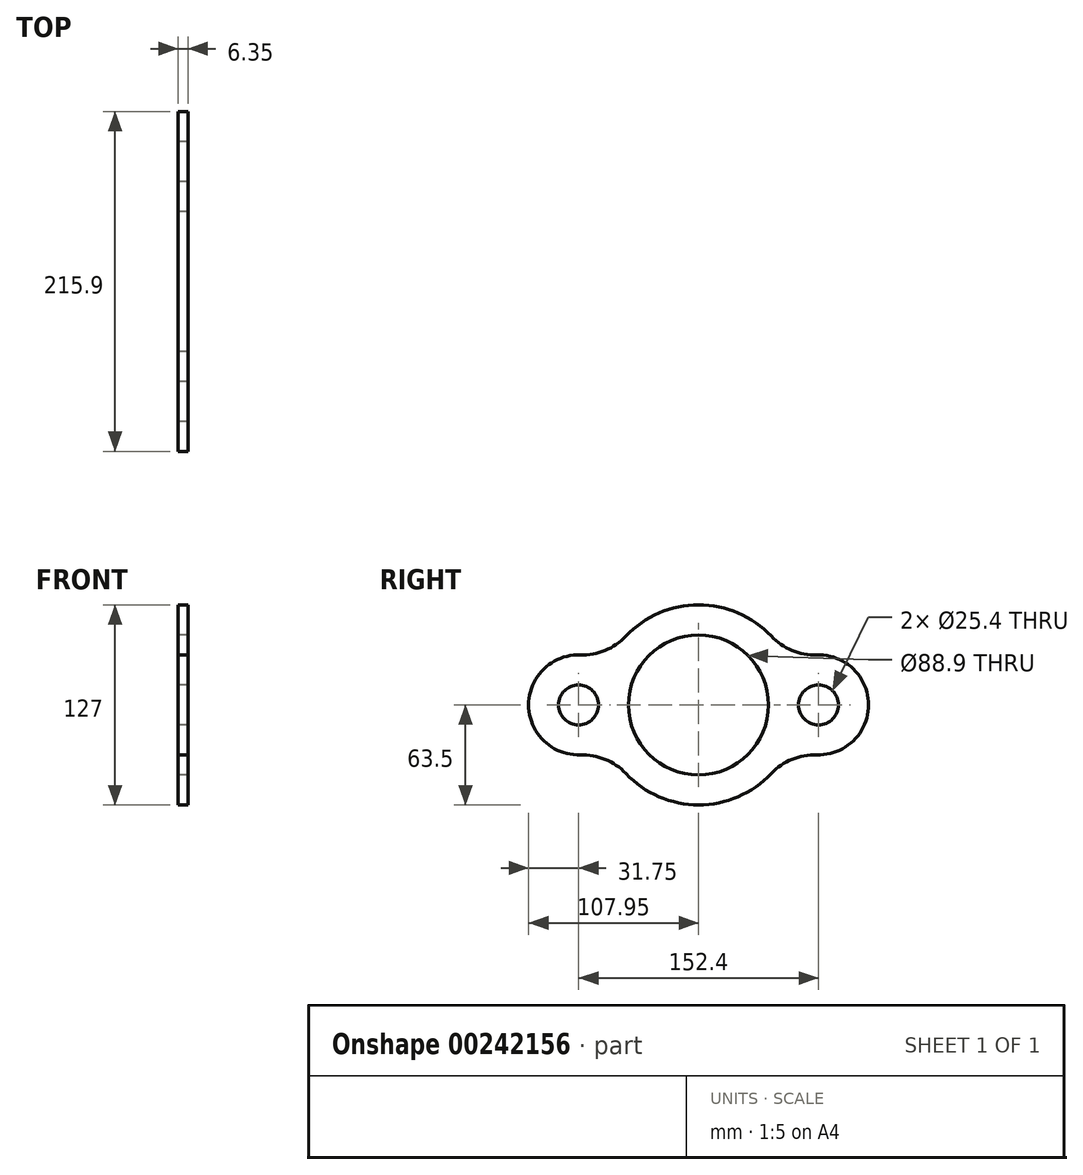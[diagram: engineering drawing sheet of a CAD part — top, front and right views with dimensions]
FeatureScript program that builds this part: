
annotation { "Feature Type Name" : "Feature", "Feature Type Description" : "" }
export const myFeature = defineFeature(function(context is Context, id is Id, definition is map)
    precondition{}
    {
        {
            var Q0;
            Q0=qCreatedBy(makeId("Right.planeOp"),FACE);
            var sketch = newSketch(context, id + "F0", { "sketchPlane" : qUnion([Q0])});
            skArc(sketch, "E0", {"start": v(46.14, 43.63) * mm, "mid": v(0, 63.5) * mm, "end": v(-46.14, 43.63) * mm});
            skCircle(sketch, "E1", {"center": v(76.2, 0) * mm, "radius": 12.7 * mm});
            skCircle(sketch, "E2", {"center": v(0, 0) * mm, "radius": 44.45 * mm});
            skArc(sketch, "E3", {"start": v(75.12, -31.73) * mm, "mid": v(107.95, 0) * mm, "end": v(75.12, 31.73) * mm});
            skCircle(sketch, "E4", {"center": v(-76.2, 0) * mm, "radius": 12.7 * mm});
            skArc(sketch, "E5", {"start": v(-75.12, 31.73) * mm, "mid": v(-107.95, 0) * mm, "end": v(-75.12, -31.73) * mm});
            skArc(sketch, "E6.trimOffspring", {"start": v(-46.14, -43.63) * mm, "mid": v(0, -63.5) * mm, "end": v(46.14, -43.63) * mm});
            skArc(sketch, "E7.filletArc", {"start": v(-75.12, 31.73) * mm, "mid": v(-59.35, 34.56) * mm, "end": v(-46.14, 43.63) * mm});
            skArc(sketch, "E8.filletArc", {"start": v(-46.14, -43.63) * mm, "mid": v(-59.35, -34.56) * mm, "end": v(-75.12, -31.73) * mm});
            skArc(sketch, "E9.filletArc", {"start": v(75.12, -31.73) * mm, "mid": v(59.35, -34.56) * mm, "end": v(46.14, -43.63) * mm});
            skArc(sketch, "E10.filletArc", {"start": v(46.14, 43.63) * mm, "mid": v(59.35, 34.56) * mm, "end": v(75.12, 31.73) * mm});
            skSolve(sketch);
        }
        {
            var Q0;
            Q0 = qSketchRegion(id + "F0", true);
            extrude(context, id + "F1", {"entities" : qUnion([Q0]), "depth" : 6.35 * mm});
        }
    });
